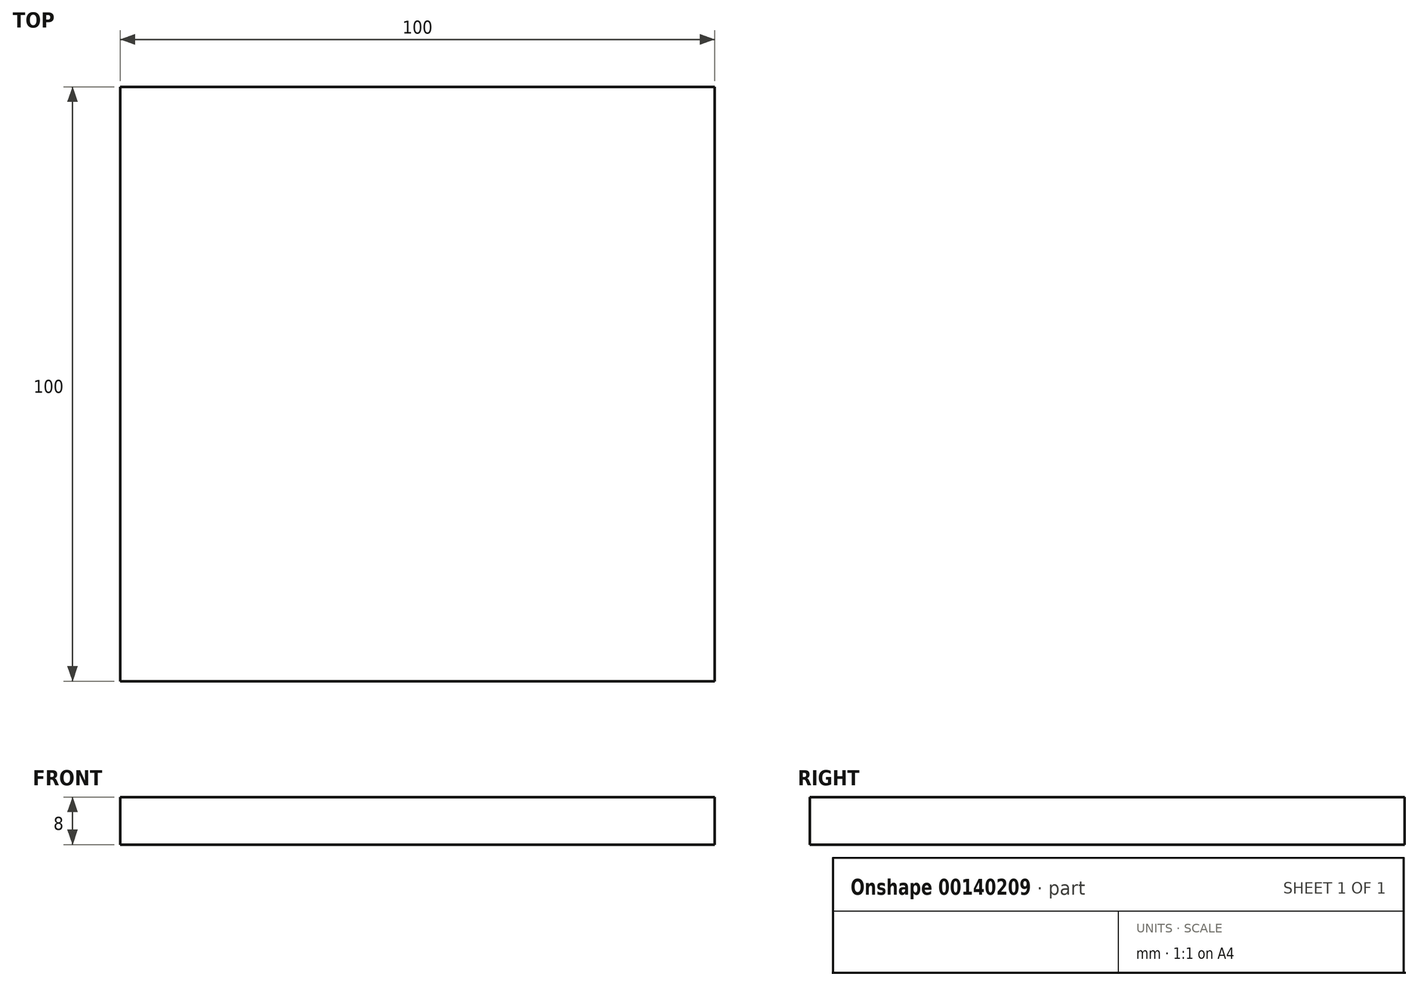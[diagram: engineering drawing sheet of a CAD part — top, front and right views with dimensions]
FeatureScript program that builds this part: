
annotation { "Feature Type Name" : "Feature", "Feature Type Description" : "" }
export const myFeature = defineFeature(function(context is Context, id is Id, definition is map)
    precondition{}
    {
        {
            var Q0;
            Q0=qCreatedBy(makeId("Top.planeOp"),FACE);
            var sketch = newSketch(context, id + "F0", { "sketchPlane" : qUnion([Q0])});
            skLineSegment(sketch, "E0.bottom", {"start": v(-50, -50) * mm, "end": v(50, -50) * mm});
            skLineSegment(sketch, "E0.top", {"start": v(-50, 50) * mm, "end": v(50, 50) * mm});
            skLineSegment(sketch, "E0.left", {"start": v(-50, -50) * mm, "end": v(-50, 50) * mm});
            skLineSegment(sketch, "E0.right", {"start": v(50, -50) * mm, "end": v(50, 50) * mm});
            skPoint(sketch, "E0.middle", {"position": v(0, 0) * mm});
            skSolve(sketch);
        }
        {
            var Q0;
            Q0=makeQuery(id+"F0.imprint","IMPRINT",FACE,{"disambiguationData":[TD([[makeQuery(id+"F0.imprint","IMPRINT",EDGE,{"derivedFrom":sQuery(id+"F0.wireOp",EDGE,"E0.bottom")}),1.0]])]});
            extrude(context, id + "F1", {"entities" : qUnion([Q0]), "oppositeDirection" : true, "depth" : 8 * mm});
        }
    });
